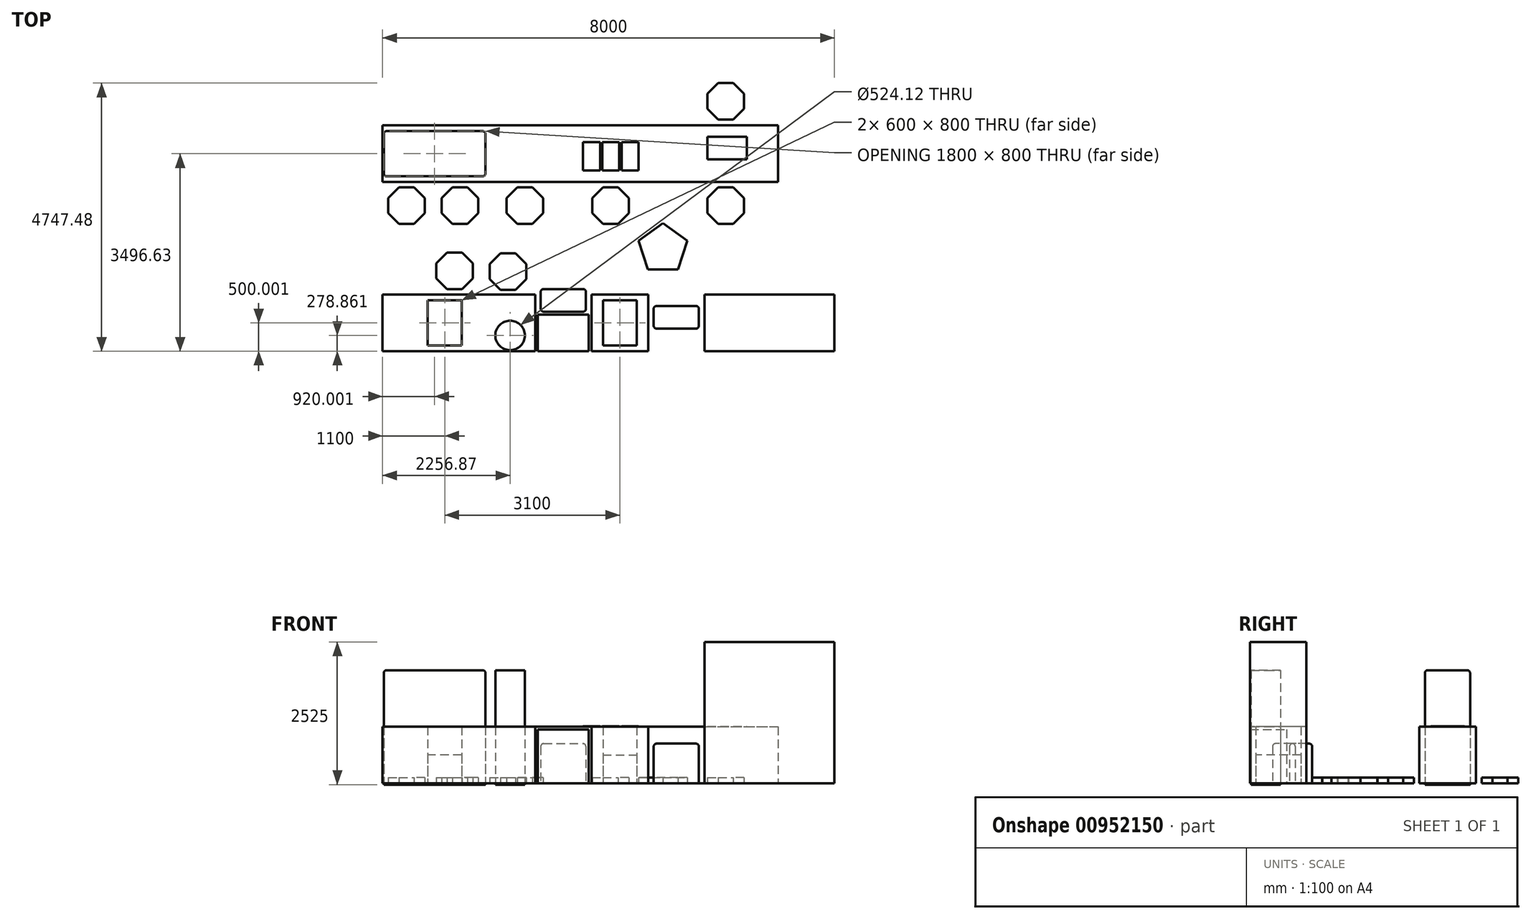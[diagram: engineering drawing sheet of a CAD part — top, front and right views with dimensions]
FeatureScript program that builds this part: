
annotation { "Feature Type Name" : "Feature", "Feature Type Description" : "" }
export const myFeature = defineFeature(function(context is Context, id is Id, definition is map)
    precondition{}
    {
        {
            var Q0;
            Q0=qCreatedBy(makeId("Top.planeOp"),FACE);
            var sketch = newSketch(context, id + "F0", { "sketchPlane" : qUnion([Q0])});
            skLineSegment(sketch, "E0.bottom", {"start": v(-3994.29, 1952.95) * mm, "end": v(4005.71, 1952.95) * mm});
            skLineSegment(sketch, "E0.left", {"start": v(-3994.29, 1952.95) * mm, "end": v(-3994.29, -2047.05) * mm});
            skLineSegment(sketch, "E0.right", {"start": v(4005.71, 1952.95) * mm, "end": v(4005.71, -2047.05) * mm});
            skLineSegment(sketch, "E1.bottom", {"start": v(-3994.29, 1952.95) * mm, "end": v(3005.71, 1952.95) * mm});
            skLineSegment(sketch, "E1.top", {"start": v(-3994.29, 952.95) * mm, "end": v(3005.71, 952.95) * mm});
            skLineSegment(sketch, "E1.left", {"start": v(-3994.29, 1952.95) * mm, "end": v(-3994.29, 952.95) * mm});
            skLineSegment(sketch, "E1.right", {"start": v(3005.71, 1952.95) * mm, "end": v(3005.71, 952.95) * mm});
            skLineSegment(sketch, "E2.bottom", {"start": v(-3994.29, -2047.05) * mm, "end": v(-1294.29, -2047.05) * mm});
            skLineSegment(sketch, "E2.top", {"start": v(-3994.29, -1047.05) * mm, "end": v(-1294.29, -1047.05) * mm});
            skLineSegment(sketch, "E2.left", {"start": v(-3994.29, -2047.05) * mm, "end": v(-3994.29, -1047.05) * mm});
            skLineSegment(sketch, "E2.right", {"start": v(-1294.29, -2047.05) * mm, "end": v(-1294.29, -1047.05) * mm});
            skLineSegment(sketch, "E3.bottom", {"start": v(-294.29, -2047.05) * mm, "end": v(705.71, -2047.05) * mm});
            skLineSegment(sketch, "E3.top", {"start": v(-294.29, -1047.05) * mm, "end": v(705.71, -1047.05) * mm});
            skLineSegment(sketch, "E3.left", {"start": v(-294.29, -2047.05) * mm, "end": v(-294.29, -1047.05) * mm});
            skLineSegment(sketch, "E3.right", {"start": v(705.71, -2047.05) * mm, "end": v(705.71, -1047.05) * mm});
            skLineSegment(sketch, "E4", {"start": v(-1294.29, -2047.05) * mm, "end": v(-294.29, -2047.05) * mm});
            skLineSegment(sketch, "E5.top", {"start": v(1705.71, -1047.05) * mm, "end": v(4005.71, -1047.05) * mm});
            skLineSegment(sketch, "E5.left", {"start": v(1705.71, -2047.05) * mm, "end": v(1705.71, -1047.05) * mm});
            skLineSegment(sketch, "E5.right", {"start": v(4005.71, -2066.24) * mm, "end": v(4005.71, -1047.05) * mm});
            skLineSegment(sketch, "E6", {"start": v(705.71, -2047.05) * mm, "end": v(1705.71, -2047.05) * mm});
            skLineSegment(sketch, "E7", {"start": v(1705.71, -2047.05) * mm, "end": v(4005.71, -2047.05) * mm});
            skLineSegment(sketch, "E8.bottom", {"start": v(-3924.29, 1849.58) * mm, "end": v(-2224.29, 1849.58) * mm});
            skLineSegment(sketch, "E8.top", {"start": v(-3924.29, 1049.58) * mm, "end": v(-2224.29, 1049.58) * mm});
            skLineSegment(sketch, "E8.left", {"start": v(-3974.29, 1799.58) * mm, "end": v(-3974.29, 1099.58) * mm});
            skLineSegment(sketch, "E8.right", {"start": v(-2174.29, 1799.58) * mm, "end": v(-2174.29, 1099.58) * mm});
            skPoint(sketch, "E9.visualSharp", {"position": v(-3974.29, 1849.58) * mm});
            skArc(sketch, "E9.filletArc", {"start": v(-3924.29, 1849.58) * mm, "mid": v(-3959.64, 1834.94) * mm, "end": v(-3974.29, 1799.58) * mm});
            skPoint(sketch, "E10.visualSharp", {"position": v(-2174.29, 1849.58) * mm});
            skArc(sketch, "E10.filletArc", {"start": v(-2174.29, 1799.58) * mm, "mid": v(-2188.93, 1834.94) * mm, "end": v(-2224.29, 1849.58) * mm});
            skPoint(sketch, "E11.visualSharp", {"position": v(-2174.29, 1049.58) * mm});
            skArc(sketch, "E11.filletArc", {"start": v(-2224.29, 1049.58) * mm, "mid": v(-2188.93, 1064.23) * mm, "end": v(-2174.29, 1099.58) * mm});
            skPoint(sketch, "E12.visualSharp", {"position": v(-3974.29, 1049.58) * mm});
            skArc(sketch, "E12.filletArc", {"start": v(-3974.29, 1099.58) * mm, "mid": v(-3959.64, 1064.23) * mm, "end": v(-3924.29, 1049.58) * mm});
            skLineSegment(sketch, "E13.bottom", {"start": v(-94.29, -1147.05) * mm, "end": v(505.71, -1147.05) * mm});
            skLineSegment(sketch, "E13.top", {"start": v(-94.29, -1947.05) * mm, "end": v(505.71, -1947.05) * mm});
            skLineSegment(sketch, "E13.left", {"start": v(-94.29, -1147.05) * mm, "end": v(-94.29, -1947.05) * mm});
            skLineSegment(sketch, "E13.right", {"start": v(505.71, -1147.05) * mm, "end": v(505.71, -1947.05) * mm});
            skLineSegment(sketch, "E14.bottom", {"start": v(-2594.29, -1147.05) * mm, "end": v(-3194.29, -1147.05) * mm});
            skLineSegment(sketch, "E14.top", {"start": v(-2594.29, -1947.05) * mm, "end": v(-3194.29, -1947.05) * mm});
            skLineSegment(sketch, "E14.left", {"start": v(-2594.29, -1147.05) * mm, "end": v(-2594.29, -1947.05) * mm});
            skLineSegment(sketch, "E14.right", {"start": v(-3194.29, -1147.05) * mm, "end": v(-3194.29, -1947.05) * mm});
            skCircle(sketch, "E15", {"center": v(-1737.42, -1768.19) * mm, "radius": 262.06 * mm});
            skCircle(sketch, "E16.cCircle", {"center": v(-2720.55, -623.31) * mm, "radius": 323.74 * mm, "construction": true});
            skLineSegment(sketch, "E16.0", {"start": v(-2396.81, -757.4) * mm, "end": v(-2586.45, -947.05) * mm});
            skLineSegment(sketch, "E16.1", {"start": v(-2586.45, -947.05) * mm, "end": v(-2854.65, -947.05) * mm});
            skLineSegment(sketch, "E16.2", {"start": v(-2854.65, -947.05) * mm, "end": v(-3044.29, -757.4) * mm});
            skLineSegment(sketch, "E16.3", {"start": v(-3044.29, -757.4) * mm, "end": v(-3044.29, -489.21) * mm});
            skLineSegment(sketch, "E16.4", {"start": v(-3044.29, -489.21) * mm, "end": v(-2854.65, -299.57) * mm});
            skLineSegment(sketch, "E16.5", {"start": v(-2854.65, -299.57) * mm, "end": v(-2586.45, -299.57) * mm});
            skLineSegment(sketch, "E16.6", {"start": v(-2586.45, -299.57) * mm, "end": v(-2396.81, -489.21) * mm});
            skLineSegment(sketch, "E16.7", {"start": v(-2396.81, -489.21) * mm, "end": v(-2396.81, -757.4) * mm});
            skPoint(sketch, "E16.0.midPoint", {"position": v(-2491.63, -852.23) * mm});
            skCircle(sketch, "E17.cCircle", {"center": v(-1773.07, -637.17) * mm, "radius": 323.74 * mm, "construction": true});
            skLineSegment(sketch, "E17.0", {"start": v(-1449.34, -771.26) * mm, "end": v(-1638.98, -960.9) * mm});
            skLineSegment(sketch, "E17.1", {"start": v(-1638.98, -960.9) * mm, "end": v(-1907.17, -960.9) * mm});
            skLineSegment(sketch, "E17.2", {"start": v(-1907.17, -960.9) * mm, "end": v(-2096.81, -771.26) * mm});
            skLineSegment(sketch, "E17.3", {"start": v(-2096.81, -771.26) * mm, "end": v(-2096.81, -503.07) * mm});
            skLineSegment(sketch, "E17.4", {"start": v(-2096.81, -503.07) * mm, "end": v(-1907.17, -313.43) * mm});
            skLineSegment(sketch, "E17.5", {"start": v(-1907.17, -313.43) * mm, "end": v(-1638.98, -313.43) * mm});
            skLineSegment(sketch, "E17.6", {"start": v(-1638.98, -313.43) * mm, "end": v(-1449.34, -503.07) * mm});
            skLineSegment(sketch, "E17.7", {"start": v(-1449.34, -503.07) * mm, "end": v(-1449.34, -771.26) * mm});
            skPoint(sketch, "E17.0.midPoint", {"position": v(-1544.16, -866.08) * mm});
            skCircle(sketch, "E18.cCircle", {"center": v(-3570.55, 529.21) * mm, "radius": 323.74 * mm, "construction": true});
            skLineSegment(sketch, "E18.0", {"start": v(-3246.81, 395.12) * mm, "end": v(-3436.45, 205.47) * mm});
            skLineSegment(sketch, "E18.1", {"start": v(-3436.45, 205.47) * mm, "end": v(-3704.65, 205.47) * mm});
            skLineSegment(sketch, "E18.2", {"start": v(-3704.65, 205.47) * mm, "end": v(-3894.29, 395.12) * mm});
            skLineSegment(sketch, "E18.3", {"start": v(-3894.29, 395.12) * mm, "end": v(-3894.29, 663.3) * mm});
            skLineSegment(sketch, "E18.4", {"start": v(-3894.29, 663.3) * mm, "end": v(-3704.65, 852.95) * mm});
            skLineSegment(sketch, "E18.5", {"start": v(-3704.65, 852.95) * mm, "end": v(-3436.45, 852.95) * mm});
            skLineSegment(sketch, "E18.6", {"start": v(-3436.45, 852.95) * mm, "end": v(-3246.81, 663.3) * mm});
            skLineSegment(sketch, "E18.7", {"start": v(-3246.81, 663.3) * mm, "end": v(-3246.81, 395.12) * mm});
            skPoint(sketch, "E18.0.midPoint", {"position": v(-3341.63, 300.3) * mm});
            skCircle(sketch, "E19.cCircle", {"center": v(-2623.07, 529.21) * mm, "radius": 323.74 * mm, "construction": true});
            skLineSegment(sketch, "E19.0", {"start": v(-2299.34, 395.12) * mm, "end": v(-2488.98, 205.47) * mm});
            skLineSegment(sketch, "E19.1", {"start": v(-2488.98, 205.47) * mm, "end": v(-2757.17, 205.47) * mm});
            skLineSegment(sketch, "E19.2", {"start": v(-2757.17, 205.47) * mm, "end": v(-2946.81, 395.12) * mm});
            skLineSegment(sketch, "E19.3", {"start": v(-2946.81, 395.12) * mm, "end": v(-2946.81, 663.3) * mm});
            skLineSegment(sketch, "E19.4", {"start": v(-2946.81, 663.3) * mm, "end": v(-2757.17, 852.95) * mm});
            skLineSegment(sketch, "E19.5", {"start": v(-2757.17, 852.95) * mm, "end": v(-2488.98, 852.95) * mm});
            skLineSegment(sketch, "E19.6", {"start": v(-2488.98, 852.95) * mm, "end": v(-2299.34, 663.3) * mm});
            skLineSegment(sketch, "E19.7", {"start": v(-2299.34, 663.3) * mm, "end": v(-2299.34, 395.12) * mm});
            skPoint(sketch, "E19.0.midPoint", {"position": v(-2394.16, 300.3) * mm});
            skCircle(sketch, "E20.cCircle", {"center": v(-1475.6, 529.21) * mm, "radius": 323.74 * mm, "construction": true});
            skLineSegment(sketch, "E20.0", {"start": v(-1151.86, 395.12) * mm, "end": v(-1341.5, 205.47) * mm});
            skLineSegment(sketch, "E20.1", {"start": v(-1341.5, 205.47) * mm, "end": v(-1609.7, 205.47) * mm});
            skLineSegment(sketch, "E20.2", {"start": v(-1609.7, 205.47) * mm, "end": v(-1799.34, 395.12) * mm});
            skLineSegment(sketch, "E20.3", {"start": v(-1799.34, 395.12) * mm, "end": v(-1799.34, 663.3) * mm});
            skLineSegment(sketch, "E20.4", {"start": v(-1799.34, 663.3) * mm, "end": v(-1609.7, 852.95) * mm});
            skLineSegment(sketch, "E20.5", {"start": v(-1609.7, 852.95) * mm, "end": v(-1341.5, 852.95) * mm});
            skLineSegment(sketch, "E20.6", {"start": v(-1341.5, 852.95) * mm, "end": v(-1151.86, 663.3) * mm});
            skLineSegment(sketch, "E20.7", {"start": v(-1151.86, 663.3) * mm, "end": v(-1151.86, 395.12) * mm});
            skPoint(sketch, "E20.0.midPoint", {"position": v(-1246.68, 300.3) * mm});
            skCircle(sketch, "E21.cCircle", {"center": v(2081.97, 529.21) * mm, "radius": 323.74 * mm, "construction": true});
            skLineSegment(sketch, "E21.0", {"start": v(2405.71, 395.12) * mm, "end": v(2216.07, 205.47) * mm});
            skLineSegment(sketch, "E21.1", {"start": v(2216.07, 205.47) * mm, "end": v(1947.88, 205.47) * mm});
            skLineSegment(sketch, "E21.2", {"start": v(1947.88, 205.47) * mm, "end": v(1758.23, 395.12) * mm});
            skLineSegment(sketch, "E21.3", {"start": v(1758.23, 395.12) * mm, "end": v(1758.23, 663.3) * mm});
            skLineSegment(sketch, "E21.4", {"start": v(1758.23, 663.3) * mm, "end": v(1947.88, 852.95) * mm});
            skLineSegment(sketch, "E21.5", {"start": v(1947.88, 852.95) * mm, "end": v(2216.07, 852.95) * mm});
            skLineSegment(sketch, "E21.6", {"start": v(2216.07, 852.95) * mm, "end": v(2405.71, 663.3) * mm});
            skLineSegment(sketch, "E21.7", {"start": v(2405.71, 663.3) * mm, "end": v(2405.71, 395.12) * mm});
            skPoint(sketch, "E21.0.midPoint", {"position": v(2310.9, 300.3) * mm});
            skCircle(sketch, "E22.cCircle", {"center": v(39.8, 529.21) * mm, "radius": 323.74 * mm, "construction": true});
            skLineSegment(sketch, "E22.0", {"start": v(363.55, 395.12) * mm, "end": v(173.9, 205.47) * mm});
            skLineSegment(sketch, "E22.1", {"start": v(173.9, 205.47) * mm, "end": v(-94.29, 205.47) * mm});
            skLineSegment(sketch, "E22.2", {"start": v(-94.29, 205.47) * mm, "end": v(-283.93, 395.12) * mm});
            skLineSegment(sketch, "E22.3", {"start": v(-283.93, 395.12) * mm, "end": v(-283.93, 663.3) * mm});
            skLineSegment(sketch, "E22.4", {"start": v(-283.93, 663.3) * mm, "end": v(-94.29, 852.95) * mm});
            skLineSegment(sketch, "E22.5", {"start": v(-94.29, 852.95) * mm, "end": v(173.9, 852.95) * mm});
            skLineSegment(sketch, "E22.6", {"start": v(173.9, 852.95) * mm, "end": v(363.55, 663.3) * mm});
            skLineSegment(sketch, "E22.7", {"start": v(363.55, 663.3) * mm, "end": v(363.55, 395.12) * mm});
            skCircle(sketch, "E23.cCircle", {"center": v(2081.97, 2376.69) * mm, "radius": 323.74 * mm, "construction": true});
            skLineSegment(sketch, "E23.0", {"start": v(2405.71, 2242.6) * mm, "end": v(2216.07, 2052.95) * mm});
            skLineSegment(sketch, "E23.1", {"start": v(2216.07, 2052.95) * mm, "end": v(1947.88, 2052.95) * mm});
            skLineSegment(sketch, "E23.2", {"start": v(1947.88, 2052.95) * mm, "end": v(1758.23, 2242.6) * mm});
            skLineSegment(sketch, "E23.3", {"start": v(1758.23, 2242.6) * mm, "end": v(1758.23, 2510.79) * mm});
            skLineSegment(sketch, "E23.4", {"start": v(1758.23, 2510.79) * mm, "end": v(1947.88, 2700.43) * mm});
            skLineSegment(sketch, "E23.5", {"start": v(1947.88, 2700.43) * mm, "end": v(2216.07, 2700.43) * mm});
            skLineSegment(sketch, "E23.6", {"start": v(2216.07, 2700.43) * mm, "end": v(2405.71, 2510.79) * mm});
            skLineSegment(sketch, "E23.7", {"start": v(2405.71, 2510.79) * mm, "end": v(2405.71, 2242.6) * mm});
            skPoint(sketch, "E23.0.midPoint", {"position": v(2310.9, 2147.77) * mm});
            skCircle(sketch, "E24.cCircle", {"center": v(970.01, -234.3) * mm, "radius": 368.32 * mm, "construction": true});
            skLineSegment(sketch, "E24.0", {"start": v(1237.61, -602.63) * mm, "end": v(702.41, -602.63) * mm});
            skLineSegment(sketch, "E24.1", {"start": v(702.41, -602.63) * mm, "end": v(537.03, -93.62) * mm});
            skLineSegment(sketch, "E24.2", {"start": v(537.03, -93.62) * mm, "end": v(970.01, 220.96) * mm});
            skLineSegment(sketch, "E24.3", {"start": v(970.01, 220.96) * mm, "end": v(1403, -93.62) * mm});
            skLineSegment(sketch, "E24.4", {"start": v(1403, -93.62) * mm, "end": v(1237.61, -602.63) * mm});
            skPoint(sketch, "E24.0.midPoint", {"position": v(970.01, -602.63) * mm});
            skLineSegment(sketch, "E25.bottom", {"start": v(855.71, -1247.05) * mm, "end": v(1555.71, -1247.05) * mm});
            skLineSegment(sketch, "E25.top", {"start": v(855.71, -1647.05) * mm, "end": v(1555.71, -1647.05) * mm});
            skLineSegment(sketch, "E25.left", {"start": v(805.71, -1297.05) * mm, "end": v(805.71, -1597.05) * mm});
            skLineSegment(sketch, "E25.right", {"start": v(1605.71, -1297.05) * mm, "end": v(1605.71, -1597.05) * mm});
            skLineSegment(sketch, "E26.bottom", {"start": v(-1144.29, -947.05) * mm, "end": v(-444.29, -947.05) * mm});
            skLineSegment(sketch, "E26.top", {"start": v(-1144.29, -1347.05) * mm, "end": v(-444.29, -1347.05) * mm});
            skLineSegment(sketch, "E26.left", {"start": v(-1194.29, -997.05) * mm, "end": v(-1194.29, -1297.05) * mm});
            skLineSegment(sketch, "E26.right", {"start": v(-394.29, -997.05) * mm, "end": v(-394.29, -1297.05) * mm});
            skPoint(sketch, "E27.visualSharp", {"position": v(-1194.29, -947.05) * mm});
            skArc(sketch, "E27.filletArc", {"start": v(-1144.29, -947.05) * mm, "mid": v(-1179.64, -961.7) * mm, "end": v(-1194.29, -997.05) * mm});
            skPoint(sketch, "E28.visualSharp", {"position": v(-394.29, -947.05) * mm});
            skArc(sketch, "E28.filletArc", {"start": v(-394.29, -997.05) * mm, "mid": v(-408.93, -961.7) * mm, "end": v(-444.29, -947.05) * mm});
            skPoint(sketch, "E29.visualSharp", {"position": v(-394.29, -1347.05) * mm});
            skArc(sketch, "E29.filletArc", {"start": v(-444.29, -1347.05) * mm, "mid": v(-408.93, -1332.4) * mm, "end": v(-394.29, -1297.05) * mm});
            skPoint(sketch, "E30.visualSharp", {"position": v(-1194.29, -1347.05) * mm});
            skArc(sketch, "E30.filletArc", {"start": v(-1194.29, -1297.05) * mm, "mid": v(-1179.64, -1332.4) * mm, "end": v(-1144.29, -1347.05) * mm});
            skPoint(sketch, "E31.visualSharp", {"position": v(805.71, -1247.05) * mm});
            skArc(sketch, "E31.filletArc", {"start": v(855.71, -1247.05) * mm, "mid": v(820.36, -1261.7) * mm, "end": v(805.71, -1297.05) * mm});
            skPoint(sketch, "E32.visualSharp", {"position": v(1605.71, -1247.05) * mm});
            skArc(sketch, "E32.filletArc", {"start": v(1605.71, -1297.05) * mm, "mid": v(1591.07, -1261.7) * mm, "end": v(1555.71, -1247.05) * mm});
            skPoint(sketch, "E33.visualSharp", {"position": v(1605.71, -1647.05) * mm});
            skArc(sketch, "E33.filletArc", {"start": v(1555.71, -1647.05) * mm, "mid": v(1591.07, -1632.4) * mm, "end": v(1605.71, -1597.05) * mm});
            skPoint(sketch, "E34.visualSharp", {"position": v(805.71, -1647.05) * mm});
            skArc(sketch, "E34.filletArc", {"start": v(805.71, -1597.05) * mm, "mid": v(820.36, -1632.4) * mm, "end": v(855.71, -1647.05) * mm});
            skLineSegment(sketch, "E35.bottom", {"start": v(-1244.29, -2047.05) * mm, "end": v(-344.29, -2047.05) * mm});
            skLineSegment(sketch, "E35.top", {"start": v(-1244.29, -1397.05) * mm, "end": v(-344.29, -1397.05) * mm});
            skLineSegment(sketch, "E35.left", {"start": v(-1244.29, -2047.05) * mm, "end": v(-1244.29, -1397.05) * mm});
            skLineSegment(sketch, "E35.right", {"start": v(-344.29, -2047.05) * mm, "end": v(-344.29, -1397.05) * mm});
            skSolve(sketch);
        }
        {
            var Q0;
            Q0=makeQuery(id+"F0.imprint","IMPRINT",FACE,{"disambiguationData":[TD([[makeQuery(id+"F0.imprint","IMPRINT",EDGE,{"derivedFrom":sQuery(id+"F0.wireOp",EDGE,"E15")}),1.0]])]});
            var Q1;
            Q1=makeQuery(id+"F0.imprint","IMPRINT",FACE,{"disambiguationData":[TD([[makeQuery(id+"F0.imprint","IMPRINT",EDGE,{"derivedFrom":sQuery(id+"F0.wireOp",EDGE,"E8.bottom")}),-1.0]])]});
            extrude(context, id + "F1", {"entities" : qUnion([Q0, Q1]), "depth" : 2000 * mm, "offsetDistance" : 25 * mm, "hasSecondDirection" : true, "secondDirectionOppositeDirection" : true, "secondDirectionDepth" : 25 * mm});
        }
        {
            var Q0;
            {var subQ1=sQuery(id+"F0.wireOp",EDGE,"E2.bottom");Q0=makeQuery(id+"F0.imprint","IMPRINT",FACE,{"disambiguationData":[TD([[makeQuery(id+"F0.imprint","IMPRINT",EDGE,{"derivedFrom":subQ1}),1.0]])]});}
            var Q1;
            {var subQ3=sQuery(id+"F0.wireOp",EDGE,"E1.top");Q1=makeQuery(id+"F0.imprint","IMPRINT",FACE,{"disambiguationData":[TD([[makeQuery(id+"F0.imprint","IMPRINT",EDGE,{"derivedFrom":subQ3}),1.0]])]});}
            var Q2;
            Q2=makeQuery(id+"F0.imprint","IMPRINT",FACE,{"disambiguationData":[TD([[makeQuery(id+"F0.imprint","IMPRINT",EDGE,{"derivedFrom":sQuery(id+"F0.wireOp",EDGE,"E3.bottom")}),1.0]])]});
            extrude(context, id + "F2", {"entities" : qUnion([Q0, Q1, Q2]), "depth" : 1000 * mm, "offsetDistance" : 25 * mm});
        }
        {
            var Q0;
            Q0=makeQuery(id+"F0.imprint","IMPRINT",FACE,{"disambiguationData":[TD([[makeQuery(id+"F0.imprint","IMPRINT",EDGE,{"derivedFrom":sQuery(id+"F0.wireOp",EDGE,"E14.bottom")}),1.0]])]});
            var Q1;
            Q1=makeQuery(id+"F0.imprint","IMPRINT",FACE,{"disambiguationData":[TD([[makeQuery(id+"F0.imprint","IMPRINT",EDGE,{"derivedFrom":sQuery(id+"F0.wireOp",EDGE,"E13.bottom")}),-1.0]])]});
            extrude(context, id + "F3", {"entities" : qUnion([Q0, Q1]), "depth" : 500 * mm, "offsetDistance" : 25 * mm});
        }
        {
            var Q0;
            Q0=makeQuery(id+"F1.opExtrude","CAP_EDGE",EDGE,{"disambiguationData":[OSD([sQuery(id+"F0.wireOp",EDGE,"E8.bottom")])],"isStart":false});
            var Q1;
            Q1=makeQuery(id+"F1.opExtrude","CAP_EDGE",EDGE,{"disambiguationData":[OSD([sQuery(id+"F0.wireOp",EDGE,"E8.left")])],"isStart":false});
            var Q2;
            Q2=makeQuery(id+"F1.opExtrude","CAP_EDGE",EDGE,{"disambiguationData":[OSD([sQuery(id+"F0.wireOp",EDGE,"E8.right")])],"isStart":false});
            var Q3;
            Q3=makeQuery(id+"F1.opExtrude","CAP_EDGE",EDGE,{"disambiguationData":[OSD([sQuery(id+"F0.wireOp",EDGE,"E8.top")])],"isStart":false});
            fillet(context, id + "F4", {"entities" : qUnion([Q0, Q1, Q2, Q3]), "radius" : 50 * mm, "tangentPropagation" : true, "allowEdgeOverflow" : false});
        }
        {
            var Q0;
            Q0=makeQuery(id+"F0.imprint","IMPRINT",FACE,{"disambiguationData":[TD([[makeQuery(id+"F0.imprint","IMPRINT",EDGE,{"derivedFrom":sQuery(id+"F0.wireOp",EDGE,"E26.bottom")}),-1.0]])]});
            var Q1;
            Q1=makeQuery(id+"F0.imprint","IMPRINT",FACE,{"disambiguationData":[TD([[makeQuery(id+"F0.imprint","IMPRINT",EDGE,{"derivedFrom":sQuery(id+"F0.wireOp",EDGE,"E25.bottom")}),-1.0]])]});
            extrude(context, id + "F5", {"entities" : qUnion([Q0, Q1]), "depth" : 700 * mm, "offsetDistance" : 25 * mm});
        }
        {
            var Q0;
            Q0=makeQuery(id+"F0.imprint","IMPRINT",FACE,{"disambiguationData":[TD([[makeQuery(id+"F0.imprint","IMPRINT",EDGE,{"derivedFrom":sQuery(id+"F0.wireOp",EDGE,"E35.top")}),-1.0]])]});
            extrude(context, id + "F6", {"entities" : qUnion([Q0]), "depth" : 950 * mm, "offsetDistance" : 25 * mm});
        }
        {
            var Q0;
            Q0=makeQuery(id+"F0.imprint","IMPRINT",FACE,{"disambiguationData":[TD([[makeQuery(id+"F0.imprint","IMPRINT",EDGE,{"derivedFrom":sQuery(id+"F0.wireOp",EDGE,"E24.0")}),-1.0]])]});
            var Q1;
            Q1=makeQuery(id+"F0.imprint","IMPRINT",FACE,{"disambiguationData":[TD([[makeQuery(id+"F0.imprint","IMPRINT",EDGE,{"derivedFrom":sQuery(id+"F0.wireOp",EDGE,"E21.0")}),-1.0]])]});
            var Q2;
            Q2=makeQuery(id+"F0.imprint","IMPRINT",FACE,{"disambiguationData":[TD([[makeQuery(id+"F0.imprint","IMPRINT",EDGE,{"derivedFrom":sQuery(id+"F0.wireOp",EDGE,"E22.0")}),-1.0]])]});
            var Q3;
            Q3=makeQuery(id+"F0.imprint","IMPRINT",FACE,{"disambiguationData":[TD([[makeQuery(id+"F0.imprint","IMPRINT",EDGE,{"derivedFrom":sQuery(id+"F0.wireOp",EDGE,"E19.0")}),-1.0]])]});
            var Q4;
            Q4=makeQuery(id+"F0.imprint","IMPRINT",FACE,{"disambiguationData":[TD([[makeQuery(id+"F0.imprint","IMPRINT",EDGE,{"derivedFrom":sQuery(id+"F0.wireOp",EDGE,"E20.0")}),-1.0]])]});
            var Q5;
            Q5=makeQuery(id+"F0.imprint","IMPRINT",FACE,{"disambiguationData":[TD([[makeQuery(id+"F0.imprint","IMPRINT",EDGE,{"derivedFrom":sQuery(id+"F0.wireOp",EDGE,"E18.0")}),-1.0]])]});
            var Q6;
            Q6=makeQuery(id+"F0.imprint","IMPRINT",FACE,{"disambiguationData":[TD([[makeQuery(id+"F0.imprint","IMPRINT",EDGE,{"derivedFrom":sQuery(id+"F0.wireOp",EDGE,"E23.0")}),-1.0]])]});
            var Q7;
            Q7=makeQuery(id+"F0.imprint","IMPRINT",FACE,{"disambiguationData":[TD([[makeQuery(id+"F0.imprint","IMPRINT",EDGE,{"derivedFrom":sQuery(id+"F0.wireOp",EDGE,"E17.0")}),-1.0]])]});
            var Q8;
            Q8=makeQuery(id+"F0.imprint","IMPRINT",FACE,{"disambiguationData":[TD([[makeQuery(id+"F0.imprint","IMPRINT",EDGE,{"derivedFrom":sQuery(id+"F0.wireOp",EDGE,"E16.0")}),-1.0]])]});
            extrude(context, id + "F7", {"entities" : qUnion([Q0, Q1, Q2, Q3, Q4, Q5, Q6, Q7, Q8]), "depth" : 100 * mm, "offsetDistance" : 25 * mm});
        }
        {
            var Q0;
            Q0=makeQuery(id+"F5.opExtrude","CAP_FACE",FACE,{"disambiguationData":[OSD([sQuery(id+"F0.wireOp",EDGE,"E25.bottom"),sQuery(id+"F0.wireOp",EDGE,"E25.top"),sQuery(id+"F0.wireOp",EDGE,"E25.left"),sQuery(id+"F0.wireOp",EDGE,"E25.right"),sQuery(id+"F0.wireOp",EDGE,"E31.filletArc"),sQuery(id+"F0.wireOp",EDGE,"E32.filletArc"),sQuery(id+"F0.wireOp",EDGE,"E33.filletArc"),sQuery(id+"F0.wireOp",EDGE,"E34.filletArc")])],"isStart":false});
            fillet(context, id + "F8", {"entities" : qUnion([Q0]), "radius" : 50 * mm, "tangentPropagation" : true, "allowEdgeOverflow" : false});
        }
        {
            var Q0;
            Q0=makeQuery(id+"F5.opExtrude","CAP_FACE",FACE,{"disambiguationData":[OSD([sQuery(id+"F0.wireOp",EDGE,"E26.bottom"),sQuery(id+"F0.wireOp",EDGE,"E26.top"),sQuery(id+"F0.wireOp",EDGE,"E26.left"),sQuery(id+"F0.wireOp",EDGE,"E26.right"),sQuery(id+"F0.wireOp",EDGE,"E27.filletArc"),sQuery(id+"F0.wireOp",EDGE,"E28.filletArc"),sQuery(id+"F0.wireOp",EDGE,"E29.filletArc"),sQuery(id+"F0.wireOp",EDGE,"E30.filletArc")])],"isStart":false});
            fillet(context, id + "F9", {"entities" : qUnion([Q0]), "radius" : 50 * mm, "tangentPropagation" : true, "allowEdgeOverflow" : false});
        }
        {
            var Q0;
            {var subQ2=sQuery(id+"F0.wireOp",EDGE,"E5.top");Q0=makeQuery(id+"F0.imprint","IMPRINT",FACE,{"disambiguationData":[TD([[makeQuery(id+"F0.imprint","IMPRINT",EDGE,{"derivedFrom":subQ2}),-1.0]])]});}
            extrude(context, id + "F10", {"entities" : qUnion([Q0]), "depth" : 2500 * mm, "offsetDistance" : 25 * mm});
        }
        {
            var Q0;
            Q0=makeQuery(id+"F2.opExtrude","CAP_FACE",FACE,{"disambiguationData":[OSD([sQuery(id+"F0.wireOp",EDGE,"E0.bottom"),sQuery(id+"F0.wireOp",EDGE,"E0.left"),sQuery(id+"F0.wireOp",EDGE,"E1.top"),sQuery(id+"F0.wireOp",EDGE,"E1.right"),sQuery(id+"F0.wireOp",EDGE,"E8.bottom"),sQuery(id+"F0.wireOp",EDGE,"E8.top"),sQuery(id+"F0.wireOp",EDGE,"E8.left"),sQuery(id+"F0.wireOp",EDGE,"E8.right"),sQuery(id+"F0.wireOp",EDGE,"E9.filletArc"),sQuery(id+"F0.wireOp",EDGE,"E10.filletArc"),sQuery(id+"F0.wireOp",EDGE,"E11.filletArc"),sQuery(id+"F0.wireOp",EDGE,"E12.filletArc")])],"isStart":false});
            var sketch = newSketch(context, id + "F11", { "sketchPlane" : qUnion([Q0])});
            skLineSegment(sketch, "E36.bottom", {"start": v(-444.29, 1652.95) * mm, "end": v(-144.29, 1652.95) * mm});
            skLineSegment(sketch, "E36.top", {"start": v(-444.29, 1152.95) * mm, "end": v(-144.29, 1152.95) * mm});
            skLineSegment(sketch, "E36.left", {"start": v(-444.29, 1652.95) * mm, "end": v(-444.29, 1152.95) * mm});
            skLineSegment(sketch, "E36.right", {"start": v(-144.29, 1652.95) * mm, "end": v(-144.29, 1152.95) * mm});
            skLineSegment(sketch, "E37.bottom", {"start": v(-104.29, 1652.95) * mm, "end": v(195.71, 1652.95) * mm});
            skLineSegment(sketch, "E37.top", {"start": v(-104.29, 1152.95) * mm, "end": v(195.71, 1152.95) * mm});
            skLineSegment(sketch, "E37.left", {"start": v(-104.29, 1652.95) * mm, "end": v(-104.29, 1152.95) * mm});
            skLineSegment(sketch, "E37.right", {"start": v(195.71, 1652.95) * mm, "end": v(195.71, 1152.95) * mm});
            skLineSegment(sketch, "E38.bottom", {"start": v(235.71, 1652.95) * mm, "end": v(535.71, 1652.95) * mm});
            skLineSegment(sketch, "E38.top", {"start": v(235.71, 1152.95) * mm, "end": v(535.71, 1152.95) * mm});
            skLineSegment(sketch, "E38.left", {"start": v(235.71, 1652.95) * mm, "end": v(235.71, 1152.95) * mm});
            skLineSegment(sketch, "E38.right", {"start": v(535.71, 1652.95) * mm, "end": v(535.71, 1152.95) * mm});
            skLineSegment(sketch, "E39.bottom", {"start": v(1755.71, 1752.95) * mm, "end": v(2455.71, 1752.95) * mm});
            skLineSegment(sketch, "E39.top", {"start": v(1755.71, 1352.95) * mm, "end": v(2455.71, 1352.95) * mm});
            skLineSegment(sketch, "E39.left", {"start": v(1755.71, 1752.95) * mm, "end": v(1755.71, 1352.95) * mm});
            skLineSegment(sketch, "E39.right", {"start": v(2455.71, 1752.95) * mm, "end": v(2455.71, 1352.95) * mm});
            skSolve(sketch);
        }
        {
            var Q0;
            Q0=makeQuery(id+"F11.imprint","IMPRINT",FACE,{"disambiguationData":[TD([[makeQuery(id+"F11.imprint","IMPRINT",EDGE,{"derivedFrom":sQuery(id+"F11.wireOp",EDGE,"E36.bottom")}),-1.0]])]});
            var Q1;
            Q1=makeQuery(id+"F11.imprint","IMPRINT",FACE,{"disambiguationData":[TD([[makeQuery(id+"F11.imprint","IMPRINT",EDGE,{"derivedFrom":sQuery(id+"F11.wireOp",EDGE,"E37.bottom")}),-1.0]])]});
            var Q2;
            Q2=makeQuery(id+"F11.imprint","IMPRINT",FACE,{"disambiguationData":[TD([[makeQuery(id+"F11.imprint","IMPRINT",EDGE,{"derivedFrom":sQuery(id+"F11.wireOp",EDGE,"E38.bottom")}),-1.0]])]});
            extrude(context, id + "F12", {"entities" : qUnion([Q0, Q1, Q2]), "operationType" : NewBodyOperationType.ADD, "depth" : 10 * mm, "offsetDistance" : 25 * mm, "hasSecondDirection" : true, "secondDirectionOppositeDirection" : true, "secondDirectionDepth" : -1 * mm});
        }
        {
            var Q0;
            Q0=makeQuery(id+"F11.imprint","IMPRINT",FACE,{"disambiguationData":[TD([[makeQuery(id+"F11.imprint","IMPRINT",EDGE,{"derivedFrom":sQuery(id+"F11.wireOp",EDGE,"E39.bottom")}),-1.0]])]});
            extrude(context, id + "F13", {"entities" : qUnion([Q0]), "depth" : 10 * mm, "offsetDistance" : 25 * mm, "hasSecondDirection" : true, "secondDirectionOppositeDirection" : true, "secondDirectionDepth" : -1 * mm});
        }
    });
